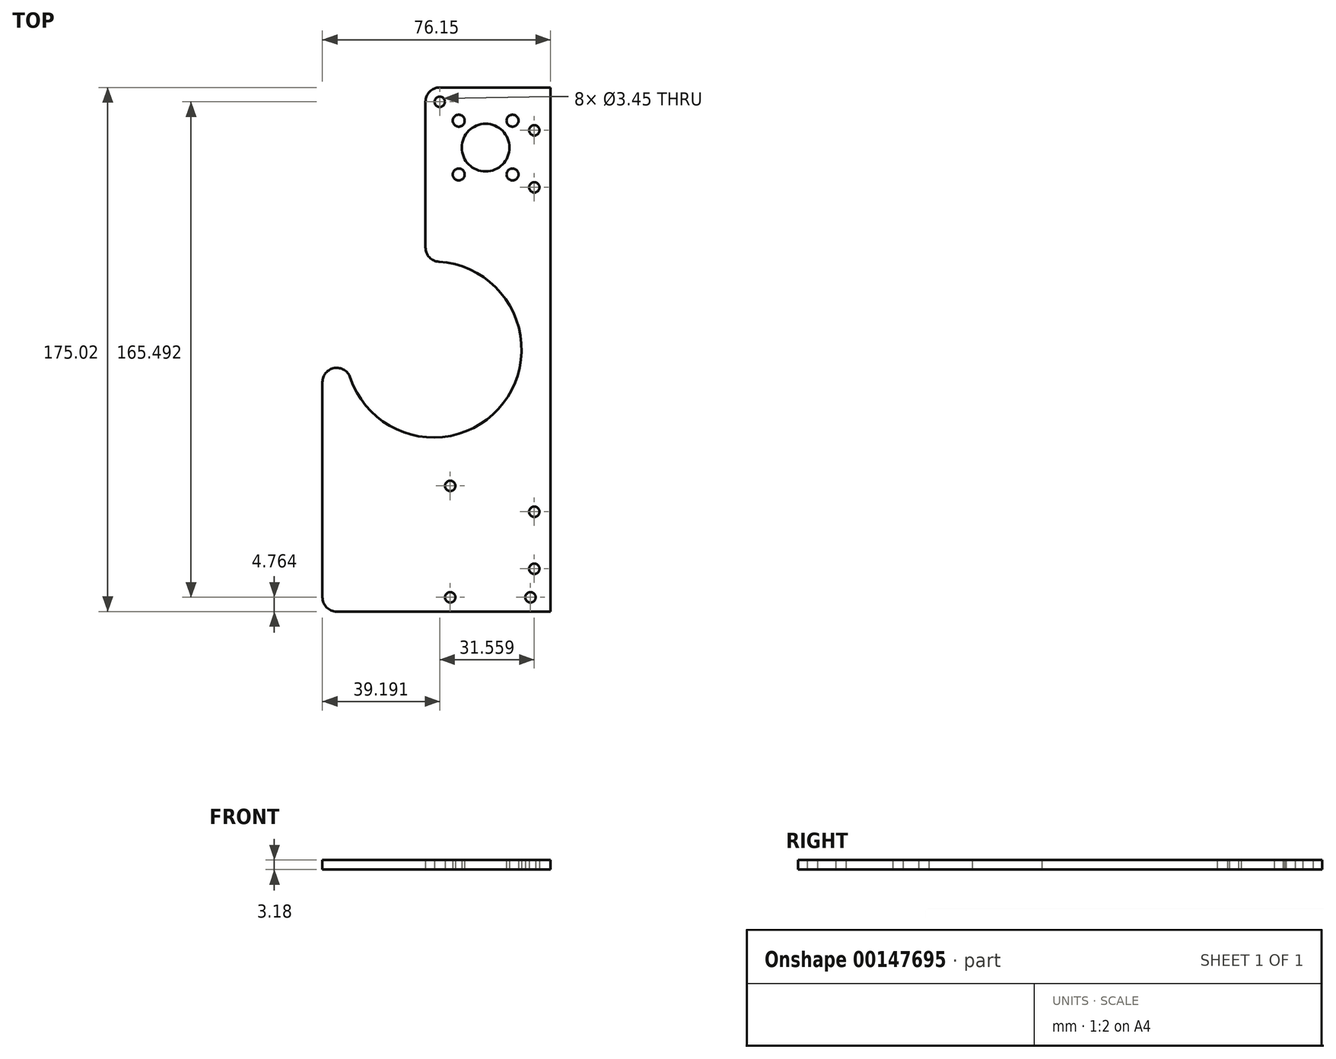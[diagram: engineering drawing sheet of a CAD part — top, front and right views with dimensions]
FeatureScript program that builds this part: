
annotation { "Feature Type Name" : "Feature", "Feature Type Description" : "" }
export const myFeature = defineFeature(function(context is Context, id is Id, definition is map)
    precondition{}
    {
        {
            var Q0;
            Q0=qCreatedBy(makeId("Top.planeOp"),FACE);
            var sketch = newSketch(context, id + "F0", { "sketchPlane" : qUnion([Q0])});
            skLineSegment(sketch, "E0.bottom", {"start": v(39.03, -87.5) * mm, "end": v(-32.35, -87.5) * mm});
            skLineSegment(sketch, "E0.top", {"start": v(39.03, 87.5) * mm, "end": v(2.07, 87.5) * mm});
            skLineSegment(sketch, "E0.left", {"start": v(39.03, -87.5) * mm, "end": v(39.03, 87.5) * mm});
            skLineSegment(sketch, "E1", {"start": v(33.63, -87.5) * mm, "end": v(33.63, -73.22) * mm, "construction": true});
            skLineSegment(sketch, "E2", {"start": v(33.63, -73.22) * mm, "end": v(33.63, -54.17) * mm, "construction": true});
            skLineSegment(sketch, "E3", {"start": v(33.63, 87.5) * mm, "end": v(33.63, 73.22) * mm, "construction": true});
            skLineSegment(sketch, "E4", {"start": v(33.63, 73.22) * mm, "end": v(33.63, 54.17) * mm, "construction": true});
            skCircle(sketch, "E5", {"center": v(33.63, 73.22) * mm, "radius": 1.73 * mm});
            skCircle(sketch, "E6", {"center": v(33.63, 54.17) * mm, "radius": 1.73 * mm});
            skCircle(sketch, "E7", {"center": v(33.63, -54.17) * mm, "radius": 1.73 * mm});
            skCircle(sketch, "E8", {"center": v(33.63, -73.22) * mm, "radius": 1.73 * mm});
            skLineSegment(sketch, "E9", {"start": v(32.35, -82.75) * mm, "end": v(5.56, -82.75) * mm, "construction": true});
            skLineSegment(sketch, "E10", {"start": v(5.56, -82.75) * mm, "end": v(5.56, -45.55) * mm, "construction": true});
            skCircle(sketch, "E11", {"center": v(5.56, -45.55) * mm, "radius": 1.73 * mm});
            skCircle(sketch, "E12", {"center": v(32.35, -82.75) * mm, "radius": 1.73 * mm});
            skArc(sketch, "E13", {"start": v(-37.12, -82.75) * mm, "mid": v(-35.72, -86.11) * mm, "end": v(-32.35, -87.5) * mm});
            skLineSegment(sketch, "E14", {"start": v(-37.12, -82.75) * mm, "end": v(-37.12, -10.87) * mm});
            skLineSegment(sketch, "E15", {"start": v(-2.7, 82.75) * mm, "end": v(-2.7, 34.07) * mm});
            skCircle(sketch, "E16", {"center": v(8.4, 76.42) * mm, "radius": 2 * mm});
            skCircle(sketch, "E17", {"center": v(17.37, 67.44) * mm, "radius": 7.96 * mm});
            skArc(sketch, "E18", {"start": v(-2.7, 34.07) * mm, "mid": v(-1.4, 30.8) * mm, "end": v(1.78, 29.31) * mm});
            skArc(sketch, "E19", {"start": v(-27.84, -9.36) * mm, "mid": v(-33.12, -6.17) * mm, "end": v(-37.12, -10.87) * mm});
            skArc(sketch, "E20", {"start": v(-27.84, -9.36) * mm, "mid": v(23.31, -17.86) * mm, "end": v(1.78, 29.31) * mm});
            skLineSegment(sketch, "E21", {"start": v(0, 0) * mm, "end": v(19.51, 0) * mm, "construction": true});
            skLineSegment(sketch, "E22", {"start": v(19.51, 0) * mm, "end": v(19.51, 0) * mm});
            skLineSegment(sketch, "E23", {"start": v(19.51, 0) * mm, "end": v(39.03, 0) * mm, "construction": true});
            skCircle(sketch, "E24", {"center": v(5.56, -82.75) * mm, "radius": 1.73 * mm});
            skLineSegment(sketch, "E25", {"start": v(32.35, -82.75) * mm, "end": v(39.03, -82.75) * mm, "construction": true});
            skLineSegment(sketch, "E26", {"start": v(32.35, -82.75) * mm, "end": v(32.35, -87.5) * mm, "construction": true});
            skLineSegment(sketch, "E27.bottom", {"start": v(8.4, 76.42) * mm, "end": v(26.36, 76.42) * mm, "construction": true});
            skLineSegment(sketch, "E27.top", {"start": v(8.4, 58.46) * mm, "end": v(26.36, 58.46) * mm, "construction": true});
            skLineSegment(sketch, "E27.left", {"start": v(8.4, 76.42) * mm, "end": v(8.4, 58.46) * mm, "construction": true});
            skLineSegment(sketch, "E27.right", {"start": v(26.36, 76.42) * mm, "end": v(26.36, 58.46) * mm, "construction": true});
            skLineSegment(sketch, "E28", {"start": v(17.37, 67.44) * mm, "end": v(8.4, 76.42) * mm, "construction": true});
            skCircle(sketch, "E29", {"center": v(8.4, 58.46) * mm, "radius": 2 * mm});
            skCircle(sketch, "E30", {"center": v(26.36, 58.46) * mm, "radius": 2 * mm});
            skCircle(sketch, "E31", {"center": v(26.36, 76.42) * mm, "radius": 2 * mm});
            skLineSegment(sketch, "E32", {"start": v(17.37, 67.44) * mm, "end": v(39.03, 67.44) * mm, "construction": true});
            skLineSegment(sketch, "E33", {"start": v(17.37, 67.44) * mm, "end": v(17.37, 87.5) * mm, "construction": true});
            skLineSegment(sketch, "E34", {"start": v(17.37, 67.44) * mm, "end": v(-2.7, 67.44) * mm, "construction": true});
            skArc(sketch, "E35", {"start": v(2.07, 87.5) * mm, "mid": v(-1.3, 86.11) * mm, "end": v(-2.7, 82.75) * mm});
            skCircle(sketch, "E36", {"center": v(2.07, 82.75) * mm, "radius": 1.73 * mm});
            skSolve(sketch);
        }
        {
            var Q0;
            Q0=qSketchRegion(id+"F0",true);
            extrude(context, id + "F1", {"entities" : qUnion([Q0]), "depth" : 3.17 * mm});
        }
    });
